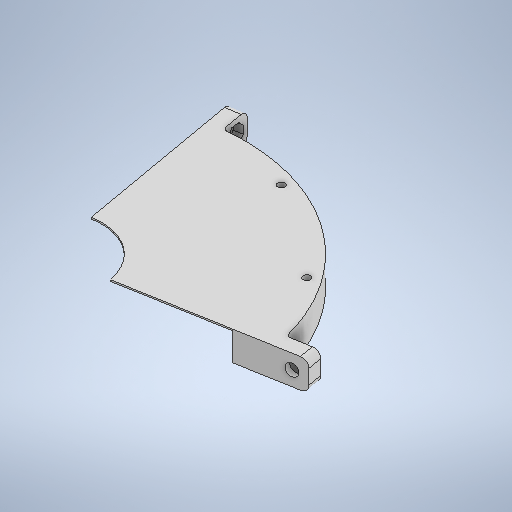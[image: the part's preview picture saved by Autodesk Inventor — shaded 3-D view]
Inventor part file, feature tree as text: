
AUTODESK INVENTOR PART (.ipt)
format: ipt  version: 2025 (Build 290162000, 162)  size: 356,864 bytes
history: native  units: in
note: dims shown in document units (in); Inventor stores cm internally (conversion verified against a paired STEP export)
features: sketch x10, extrude x6, hole x3, fillet x2
ambient origin geometry x8: Origin, YZ Plane, XZ Plane, XY Plane, X Axis, Y Axis, Z Axis, Center Point
bodies: Solid1 (feature_tree)
feature tree (21):
  extrude  "Extrusion1"  Depth=8.6614in
  extrude  "Extrusion2"  Depth=0.7874in
  hole  "Hole1"  [1 undecoded]
  extrude  "Extrusion3"  Depth=0.1969in TaperAngle=360.0deg
  extrude  "Extrusion4"  Depth=5.315in
  fillet  "Fillet1"  Radius=5.315in
  extrude  "Extrusion5"  Depth=0.6871in
  fillet  "Fillet2"  [1 undecoded]
  extrude  "Extrusion6"  Depth=0.7874in
  hole  "Hole2"  [1 undecoded]
  hole  "Hole3"  [1 undecoded]
  sketch  "Sketch1"  dims[d0=10.6299in d1=8.6614in]
  sketch  "Sketch2"  dims[d5=0.0394in d6=0.0in d7=10.0394in]
  sketch  "Sketch3"  dims[d8=0.1969in d9=3.937in d11=360.0deg]
  sketch  "Sketch Circular Pattern1"  dims[d2=0.7874in d3=0.0in d4=2.9528in]
  sketch  "Sketch4"  dims[d13=0.1969in d14=0.2362in d15=0.1575in d16=0.0787in d17=90.0deg d18=0.315in d19=0.8108in d20=10.6299in d21=5.315in]
  sketch  "Sketch5"  dims[d22=0.0687in d23=0.6871in d24=0.0in d25=0.0in]
  sketch  "Sketch6"  dims[d26=0.8858in d27=0.7874in]
  sketch  "Sketch7"  dims[d28=0.7874in d29=0.1969in]
  sketch  "Sketch8"  dims[d30=0.3937in d31=0.0in d32=0.0984in]
  sketch  "Sketch9"  dims[d33=0.8858in d34=0.7874in d35=0.7874in d36=0.1969in d37=0.3937in d38=0.0in d39=0.0984in d40=0.3937in d41=0.3937in d42=0.5197in d43=0.2362in d44=0.0in d45=0.3937in d46=0.3937in d47=0.3228in d48=0.2362in d49=0.1575in d50=0.0787in d51=90.0deg d52=0.315in d53=0.8108in d54=0.3937in d55=0.3937in d56=0.3228in d57=0.2362in d58=0.5197in d59=0.2362in d60=90.0deg d61=0.315in d62=0.8108in]
note: 4 required parameter values undecoded (feature->parameter linkage not recoverable at this tier; creation-order binding heuristic only, values carry confidence <= 0.55)
